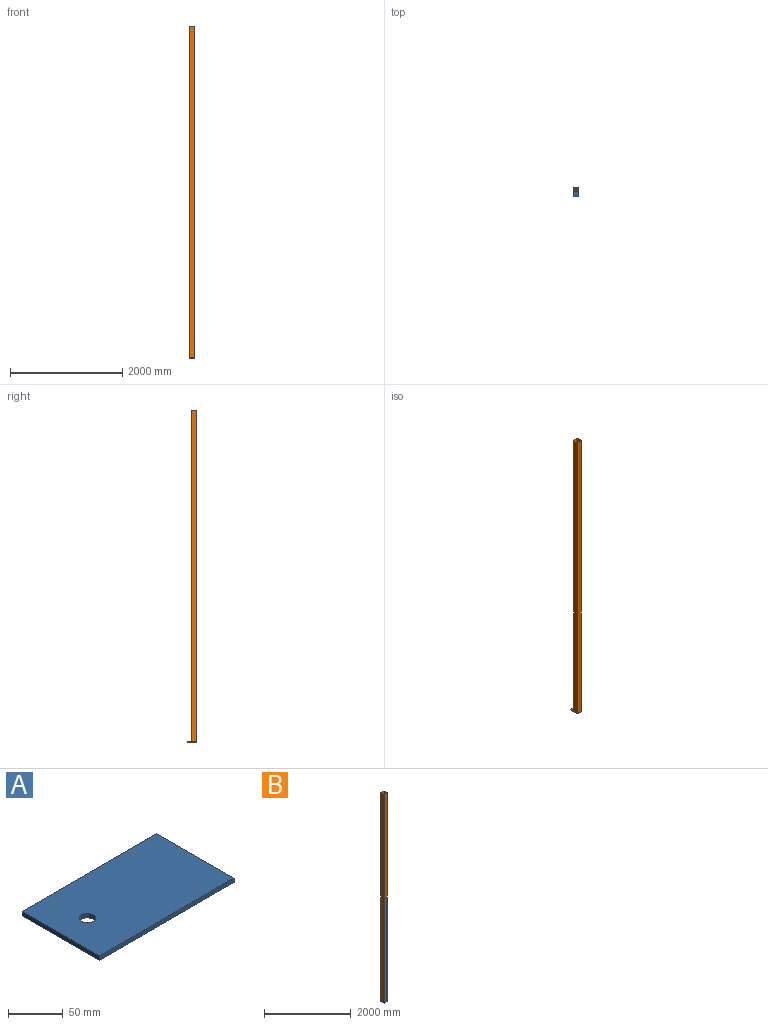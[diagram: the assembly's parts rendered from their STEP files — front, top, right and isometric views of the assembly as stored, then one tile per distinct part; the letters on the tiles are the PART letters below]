
ASSEMBLY  parts=2 mates=1
PART A: 7 faces, bbox 175x100x5 mm
  f0: plane 100x5mm, normal (1,0,0), area 500mm2, adj f1,f3,f4,f5
  f1: plane 175x5mm, normal (0,1,0), area 875mm2, adj f0,f2,f4,f5
  f2: plane 100x5mm, normal (-1,0,0), area 500mm2, adj f1,f3,f4,f5
  f3: plane 175x5mm, normal (0,-1,0), area 875mm2, adj f0,f2,f4,f5
  f4: plane 175x100mm, normal (0,0,1), area 17323.3mm2, adj f0,f1,f2,f3,f6
  f5: plane 175x100mm, normal (0,0,-1), area 17323.3mm2, adj f0,f1,f2,f3,f6
  f6: cylinder r=7.5mm len=15mm, axis (0,0,1), area 235.6mm2, adj f4,f5
PART B: 10 faces, bbox 100x100x5900 mm
  f0: plane 5900x100mm, normal (1,0,0), area 590000mm2, adj f1,f7,f8,f9
  f1: plane 5900x100mm, normal (0,1,0), area 590000mm2, adj f0,f2,f8,f9
  f2: plane 5900x100mm, normal (-1,0,0), area 590000mm2, adj f1,f7,f8,f9
  f3: plane 5900x94mm, normal (0,-1,0), area 554600mm2, adj f4,f6,f8,f9
  f4: plane 5900x94mm, normal (-1,0,0), area 554600mm2, adj f3,f5,f8,f9
  f5: plane 5900x94mm, normal (0,1,0), area 554600mm2, adj f4,f6,f8,f9
  f6: plane 5900x94mm, normal (1,0,0), area 554600mm2, adj f3,f5,f8,f9
  f7: plane 5900x100mm, normal (0,-1,0), area 590000mm2, adj f0,f2,f8,f9
  f8: plane 100x100mm, normal (0,0,1), area 1164mm2, adj f0,f1,f2,f3,f4,f5,f6,f7
  f9: plane 100x100mm, normal (0,0,-1), area 1164mm2, adj f0,f1,f2,f3,f4,f5,f6,f7
PLACE A rot(axis=(0,0,-1),90deg) t=(-55.06,6.96,-2953.13)mm
PLACE B t=(-55.06,-30.54,-2948.13)mm
MATE fastened A.f4 <-> B.f9  axis (0,0,1) through (-105.06,-80.54,-2948.13)mm
